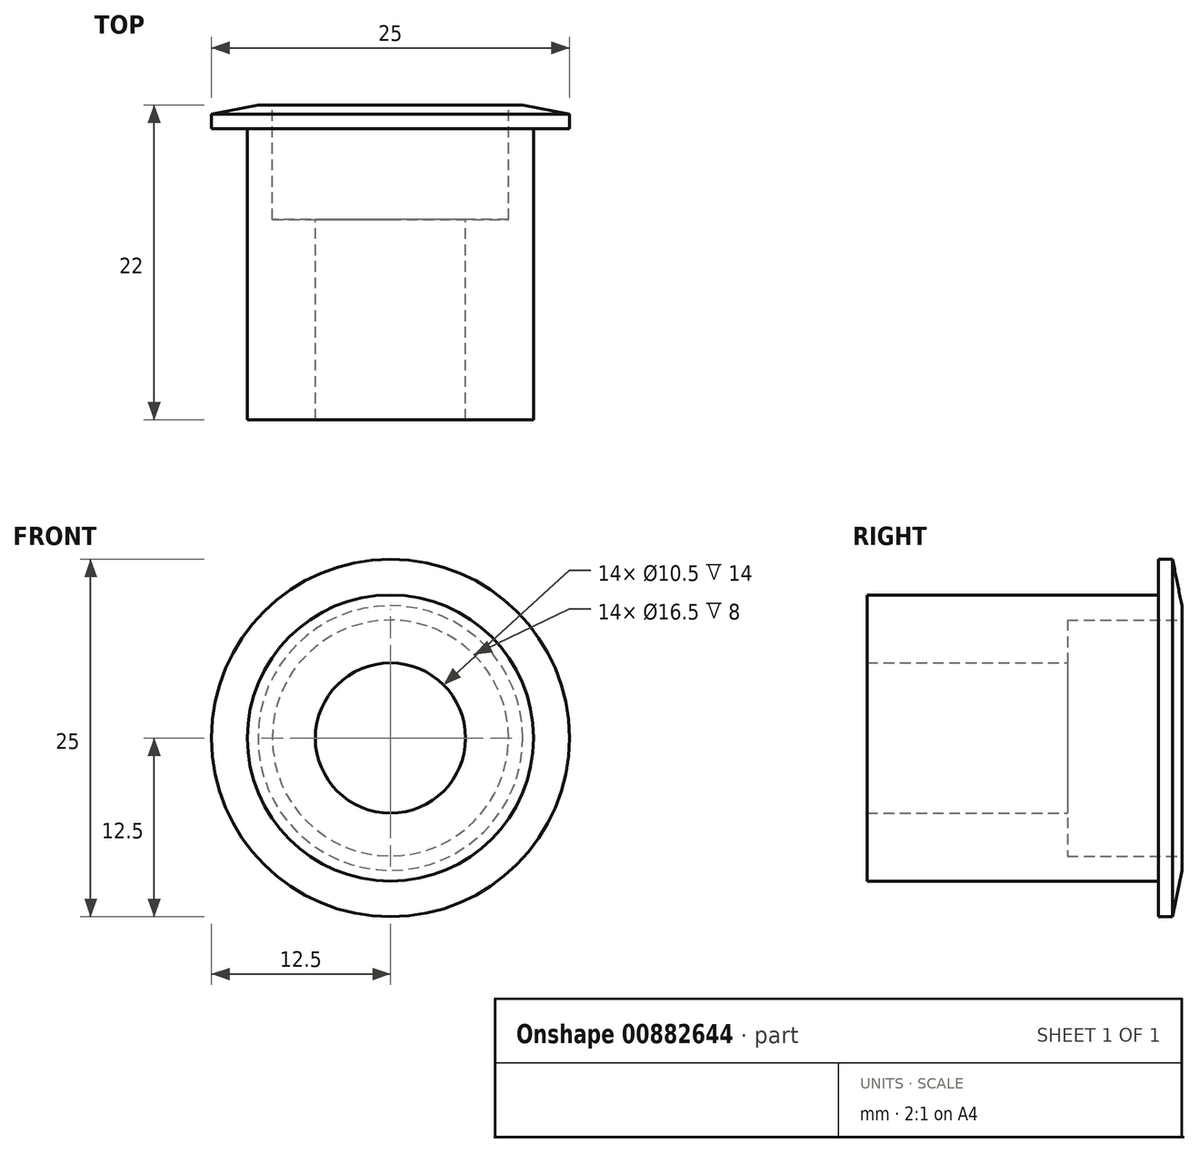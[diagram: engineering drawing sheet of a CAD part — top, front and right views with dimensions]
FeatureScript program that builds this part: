
annotation { "Feature Type Name" : "Feature", "Feature Type Description" : "" }
export const myFeature = defineFeature(function(context is Context, id is Id, definition is map)
    precondition{}
    {
        {
            var Q0;
            Q0=qCreatedBy(makeId("Right.planeOp"),FACE);
            var sketch = newSketch(context, id + "F0", { "sketchPlane" : qUnion([Q0])});
            skLineSegment(sketch, "E0", {"start": v(7.98, 0) * mm, "end": v(-14.72, 0) * mm, "construction": true});
            skLineSegment(sketch, "E1", {"start": v(-1.65, 12.5) * mm, "end": v(-1.65, 10) * mm});
            skLineSegment(sketch, "E2", {"start": v(-1.65, 10) * mm, "end": v(-22, 10) * mm});
            skLineSegment(sketch, "E3", {"start": v(-22, 10) * mm, "end": v(-22, 5.25) * mm});
            skLineSegment(sketch, "E4", {"start": v(-22, 5.25) * mm, "end": v(-8, 5.25) * mm});
            skLineSegment(sketch, "E5", {"start": v(0, 8.25) * mm, "end": v(0, 9.25) * mm});
            skLineSegment(sketch, "E6", {"start": v(0, 9.25) * mm, "end": v(-0.65, 12.5) * mm});
            skLineSegment(sketch, "E7", {"start": v(-0.65, 12.5) * mm, "end": v(-1.65, 12.5) * mm});
            skLineSegment(sketch, "E8", {"start": v(0, 8.25) * mm, "end": v(-8, 8.25) * mm});
            skLineSegment(sketch, "E9", {"start": v(-8, 8.25) * mm, "end": v(-8, 5.25) * mm});
            skSolve(sketch);
        }
        {
            var Q0;
            Q0 = qSketchRegion(id + "F0", true);
            var Q1;
            Q1=sQuery(id+"F0.wireOp",EDGE,"E0");
            revolve(context, id + "F1", {"surfaceOperationType" : NewSurfaceOperationType.NEW, "entities" : qUnion([Q0]), "axis" : qUnion([Q1]), "revolveType" : RevolveType.FULL});
        }
    });
